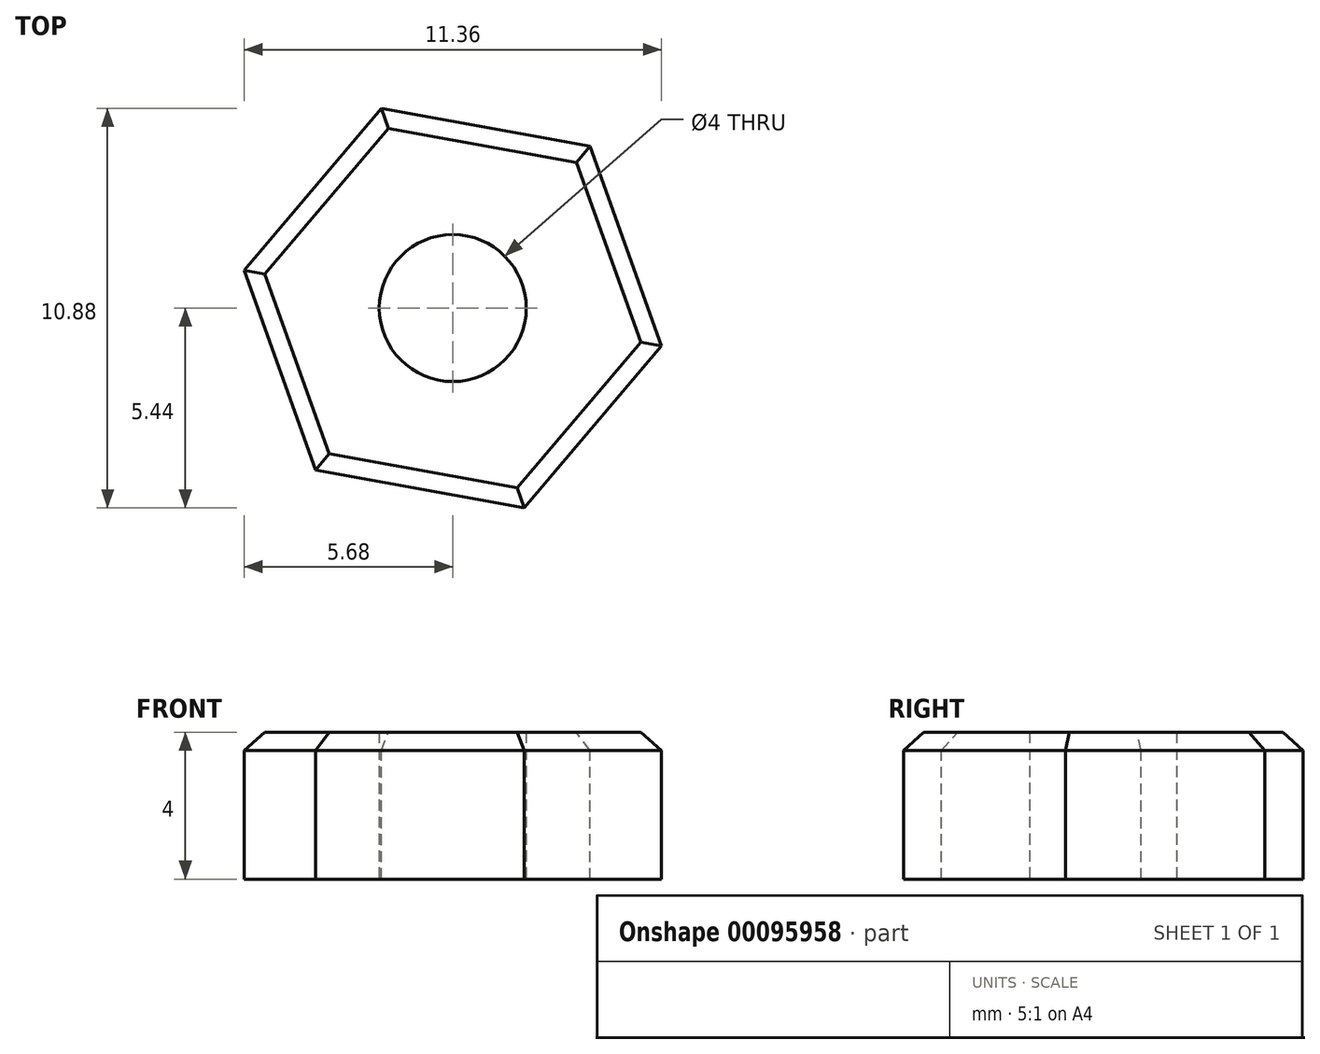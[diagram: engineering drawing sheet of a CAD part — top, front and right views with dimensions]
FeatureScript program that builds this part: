
annotation { "Feature Type Name" : "Feature", "Feature Type Description" : "" }
export const myFeature = defineFeature(function(context is Context, id is Id, definition is map)
    precondition{}
    {
        {
            var Q0;
            Q0=qCreatedBy(makeId("Right.planeOp"),FACE);
            var sketch = newSketch(context, id + "F0", { "sketchPlane" : qUnion([Q0])});
            skArc(sketch, "E0", {"start": v(4, 0) * mm, "mid": v(0, 4) * mm, "end": v(-4, 0) * mm});
            skLineSegment(sketch, "E1", {"start": v(-4, 0) * mm, "end": v(4, 0) * mm});
            skSolve(sketch);
        }
        {
            var Q0;
            Q0=makeQuery(id+"F0.imprint","IMPRINT",FACE,{"disambiguationData":[TD([[makeQuery(id+"F0.imprint","IMPRINT",EDGE,{"derivedFrom":sQuery(id+"F0.wireOp",EDGE,"E0")}),1.0]])]});
            var Q1;
            Q1=sQuery(id+"F0.wireOp",EDGE,"E0");
            var Q2;
            Q2=sQuery(id+"F0.wireOp",EDGE,"E1");
            revolve(context, id + "F1", {"bodyType" : ToolBodyType.SURFACE, "entities" : qUnion([Q0]), "surfaceEntities" : qUnion([Q1]), "axis" : qUnion([Q2]), "revolveType" : RevolveType.TWO_DIRECTIONS, "angle" : 90 * degree, "angleBack" : 270 * degree});
        }
        {
            var Q0;
            Q0=qCreatedBy(makeId("Top.planeOp"),FACE);
            var sketch = newSketch(context, id + "F2", { "sketchPlane" : qUnion([Q0])});
            skCircle(sketch, "E2.cCircle", {"center": v(0, 0) * mm, "radius": 5.77 * mm, "construction": true});
            skLineSegment(sketch, "E2.0", {"start": v(3.73, 4.4) * mm, "end": v(5.68, -1.03) * mm});
            skLineSegment(sketch, "E2.1", {"start": v(5.68, -1.03) * mm, "end": v(1.95, -5.44) * mm});
            skLineSegment(sketch, "E2.2", {"start": v(1.95, -5.44) * mm, "end": v(-3.73, -4.4) * mm});
            skLineSegment(sketch, "E2.3", {"start": v(-3.73, -4.4) * mm, "end": v(-5.68, 1.03) * mm});
            skLineSegment(sketch, "E2.4", {"start": v(-5.68, 1.03) * mm, "end": v(-1.95, 5.44) * mm});
            skLineSegment(sketch, "E2.5", {"start": v(-1.95, 5.44) * mm, "end": v(3.73, 4.4) * mm});
            skSolve(sketch);
        }
        {
            var Q0;
            Q0=makeQuery(id+"F2.imprint","IMPRINT",FACE,{"disambiguationData":[TD([[makeQuery(id+"F2.imprint","IMPRINT",EDGE,{"derivedFrom":sQuery(id+"F2.wireOp",EDGE,"E2.0")}),-1.0]])]});
            extrude(context, id + "F3", {"entities" : qUnion([Q0]), "oppositeDirection" : true, "depth" : 4 * mm});
        }
        {
            var Q0;
            Q0=makeQuery(id+"F3.opExtrude","CAP_FACE",FACE,{"disambiguationData":[OSD([sQuery(id+"F2.wireOp",EDGE,"E2.0"),sQuery(id+"F2.wireOp",EDGE,"E2.1"),sQuery(id+"F2.wireOp",EDGE,"E2.2"),sQuery(id+"F2.wireOp",EDGE,"E2.3"),sQuery(id+"F2.wireOp",EDGE,"E2.4"),sQuery(id+"F2.wireOp",EDGE,"E2.5")])],"isStart":false});
            var sketch = newSketch(context, id + "F4", { "sketchPlane" : qUnion([Q0])});
            skCircle(sketch, "E3", {"center": v(0, 0) * mm, "radius": 2 * mm});
            skSolve(sketch);
        }
        {
            var Q0;
            Q0 = qSketchRegion(id + "F4", true);
            extrude(context, id + "F5", {"entities" : qUnion([Q0]), "operationType" : NewBodyOperationType.REMOVE, "oppositeDirection" : true, "depth" : 4 * mm});
        }
        {
            var Q0;
            Q0=makeQuery(id+"F3.opExtrude","CAP_EDGE",EDGE,{"disambiguationData":[OSD([sQuery(id+"F2.wireOp",EDGE,"E2.2")])],"isStart":true});
            var Q1;
            Q1=makeQuery(id+"F3.opExtrude","CAP_EDGE",EDGE,{"disambiguationData":[OSD([sQuery(id+"F2.wireOp",EDGE,"E2.1")])],"isStart":true});
            var Q2;
            Q2=makeQuery(id+"F3.opExtrude","CAP_EDGE",EDGE,{"disambiguationData":[OSD([sQuery(id+"F2.wireOp",EDGE,"E2.0")])],"isStart":true});
            var Q3;
            Q3=makeQuery(id+"F3.opExtrude","CAP_EDGE",EDGE,{"disambiguationData":[OSD([sQuery(id+"F2.wireOp",EDGE,"E2.5")])],"isStart":true});
            var Q4;
            Q4=makeQuery(id+"F3.opExtrude","CAP_EDGE",EDGE,{"disambiguationData":[OSD([sQuery(id+"F2.wireOp",EDGE,"E2.4")])],"isStart":true});
            var Q5;
            Q5=makeQuery(id+"F3.opExtrude","CAP_EDGE",EDGE,{"disambiguationData":[OSD([sQuery(id+"F2.wireOp",EDGE,"E2.3")])],"isStart":true});
            chamfer(context, id + "F6", {"entities" : qUnion([Q0, Q1, Q2, Q3, Q4, Q5]), "width" : .5 * mm, "tangentPropagation" : true});
        }
    });
